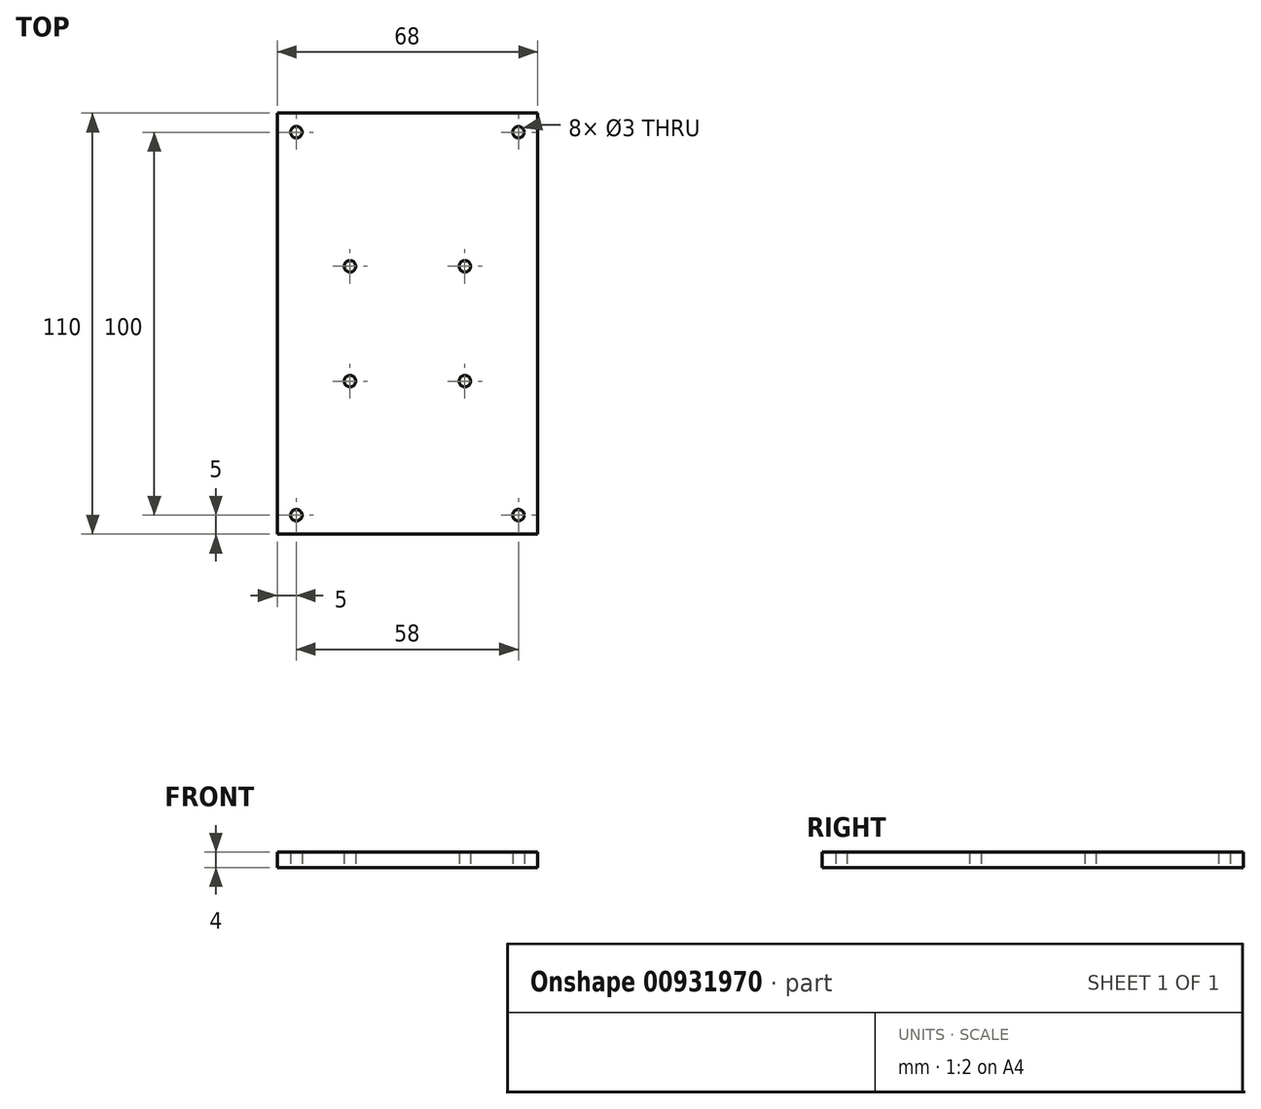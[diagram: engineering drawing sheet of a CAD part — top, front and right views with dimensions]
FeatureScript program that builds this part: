
annotation { "Feature Type Name" : "Feature", "Feature Type Description" : "" }
export const myFeature = defineFeature(function(context is Context, id is Id, definition is map)
    precondition{}
    {
        {
            var Q0;
            Q0=qCreatedBy(makeId("Top.planeOp"),FACE);
            var sketch = newSketch(context, id + "F0", { "sketchPlane" : qUnion([Q0])});
            skLineSegment(sketch, "E0.bottom", {"start": v(-34, 55) * mm, "end": v(34, 55) * mm});
            skLineSegment(sketch, "E0.top", {"start": v(-34, -55) * mm, "end": v(34, -55) * mm});
            skLineSegment(sketch, "E0.left", {"start": v(-34, 55) * mm, "end": v(-34, -55) * mm});
            skLineSegment(sketch, "E0.right", {"start": v(34, 55) * mm, "end": v(34, -55) * mm});
            skPoint(sketch, "E1", {"position": v(34, 0) * mm});
            skPoint(sketch, "E2", {"position": v(-34, 0) * mm});
            skPoint(sketch, "E3", {"position": v(0, -55) * mm});
            skPoint(sketch, "E4", {"position": v(0, 55) * mm});
            skCircle(sketch, "E5", {"center": v(-29, 50) * mm, "radius": 1.5 * mm});
            skCircle(sketch, "E6", {"center": v(29, 50) * mm, "radius": 1.5 * mm});
            skCircle(sketch, "E7", {"center": v(29, -50) * mm, "radius": 1.5 * mm});
            skCircle(sketch, "E8", {"center": v(-29, -50) * mm, "radius": 1.5 * mm});
            skLineSegment(sketch, "E9", {"start": v(-29, 50) * mm, "end": v(29, 50) * mm});
            skLineSegment(sketch, "E10", {"start": v(29, -50) * mm, "end": v(29, 50) * mm});
            skPoint(sketch, "E11", {"position": v(0, 50) * mm});
            skPoint(sketch, "E12", {"position": v(29, 0) * mm});
            skCircle(sketch, "E13", {"center": v(-15, 15) * mm, "radius": 1.5 * mm});
            skCircle(sketch, "E14", {"center": v(15, 15) * mm, "radius": 1.5 * mm});
            skCircle(sketch, "E15", {"center": v(15, -15) * mm, "radius": 1.5 * mm});
            skCircle(sketch, "E16", {"center": v(-15, -15) * mm, "radius": 1.5 * mm});
            skLineSegment(sketch, "E17", {"start": v(-15, 15) * mm, "end": v(15, 15) * mm});
            skLineSegment(sketch, "E18", {"start": v(15, -15) * mm, "end": v(15, 15) * mm});
            skPoint(sketch, "E19", {"position": v(0, 15) * mm});
            skPoint(sketch, "E20", {"position": v(15, 0) * mm});
            skSolve(sketch);
        }
        {
            var Q0;
            Q0 = qSketchRegion(id + "F0", true);
            extrude(context, id + "F1", {"entities" : qUnion([Q0]), "depth" : 4 * mm, "offsetDistance" : 25 * mm});
        }
    });
